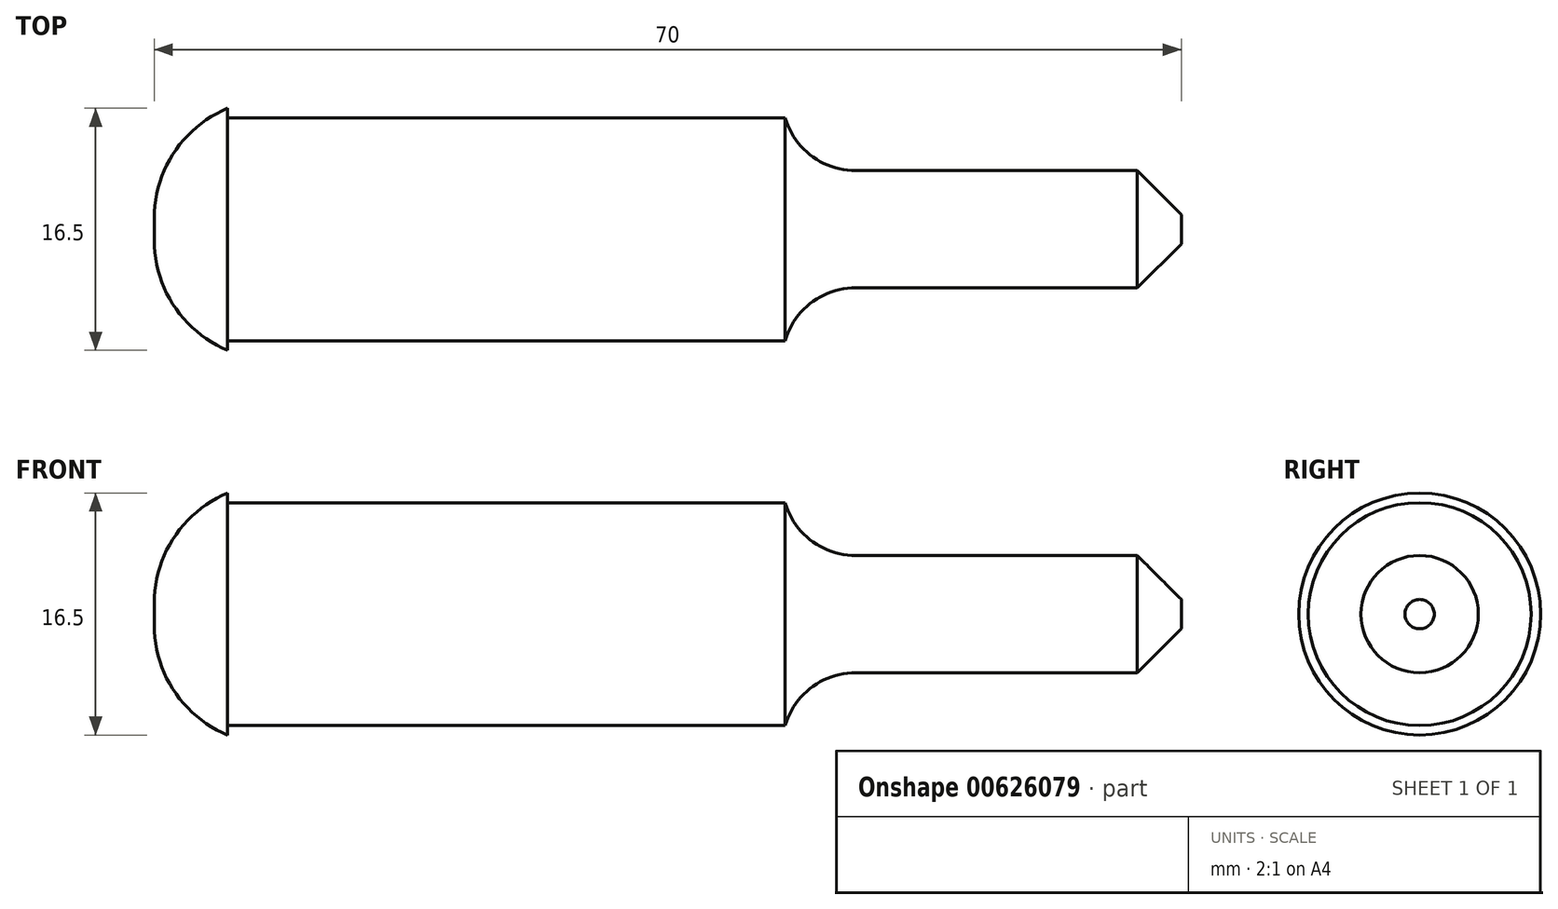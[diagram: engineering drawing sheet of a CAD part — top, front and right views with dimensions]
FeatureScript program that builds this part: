
annotation { "Feature Type Name" : "Feature", "Feature Type Description" : "" }
export const myFeature = defineFeature(function(context is Context, id is Id, definition is map)
    precondition{}
    {
        {
            var Q0;
            Q0=qCreatedBy(makeId("Front.planeOp"),FACE);
            var sketch = newSketch(context, id + "F0", { "sketchPlane" : qUnion([Q0])});
            skLineSegment(sketch, "E0", {"start": v(0, 0) * mm, "end": v(70, 0) * mm});
            skLineSegment(sketch, "E1", {"start": v(70, 0) * mm, "end": v(70, 4) * mm});
            skLineSegment(sketch, "E2", {"start": v(70, 4) * mm, "end": v(43, 4) * mm});
            skLineSegment(sketch, "E3", {"start": v(43, 4) * mm, "end": v(43, 7.6) * mm});
            skLineSegment(sketch, "E4", {"start": v(43, 7.6) * mm, "end": v(5, 7.6) * mm});
            skLineSegment(sketch, "E5", {"start": v(0, 8.25) * mm, "end": v(0, 0) * mm});
            skLineSegment(sketch, "E6", {"start": v(5, 7.6) * mm, "end": v(5, 8.25) * mm});
            skLineSegment(sketch, "E7", {"start": v(5, 8.25) * mm, "end": v(0, 8.25) * mm});
            skSolve(sketch);
        }
        {
            var Q0;
            Q0=makeQuery(id+"F0.imprint","IMPRINT",FACE,{"disambiguationData":[TD([[makeQuery(id+"F0.imprint","IMPRINT",EDGE,{"derivedFrom":sQuery(id+"F0.wireOp",EDGE,"E0")}),1.0]])]});
            var Q1;
            Q1=sQuery(id+"F0.wireOp",EDGE,"E0");
            revolve(context, id + "F1", {"entities" : qUnion([Q0]), "axis" : qUnion([Q1]), "revolveType" : RevolveType.FULL});
        }
        {
            var Q0;
            Q0=makeQuery(id+"F1.opRevolve","SWEPT_EDGE",EDGE,{"disambiguationData":[OSD([sQuery(id+"F0.wireOp",EDGE,"E2"),sQuery(id+"F0.wireOp",EDGE,"E3")])]});
            fillet(context, id + "F2", {"entities" : qUnion([Q0]), "radius" : 5 * mm, "tangentPropagation" : true, "allowEdgeOverflow" : false});
        }
        {
            var Q0;
            Q0=makeQuery(id+"F1.opRevolve","SWEPT_EDGE",EDGE,{"disambiguationData":[OSD([sQuery(id+"F0.wireOp",EDGE,"E1"),sQuery(id+"F0.wireOp",EDGE,"E2")])]});
            chamfer(context, id + "F3", {"entities" : qUnion([Q0]), "width" : 3 * mm, "tangentPropagation" : true});
        }
        {
            var Q0;
            Q0=makeQuery(id+"F1.opRevolve","SWEPT_EDGE",EDGE,{"disambiguationData":[OSD([sQuery(id+"F0.wireOp",EDGE,"E5"),sQuery(id+"F0.wireOp",EDGE,"E7")])]});
            fillet(context, id + "F4", {"entities" : qUnion([Q0]), "radius" : 8.1 * mm, "tangentPropagation" : true, "allowEdgeOverflow" : false});
        }
    });
